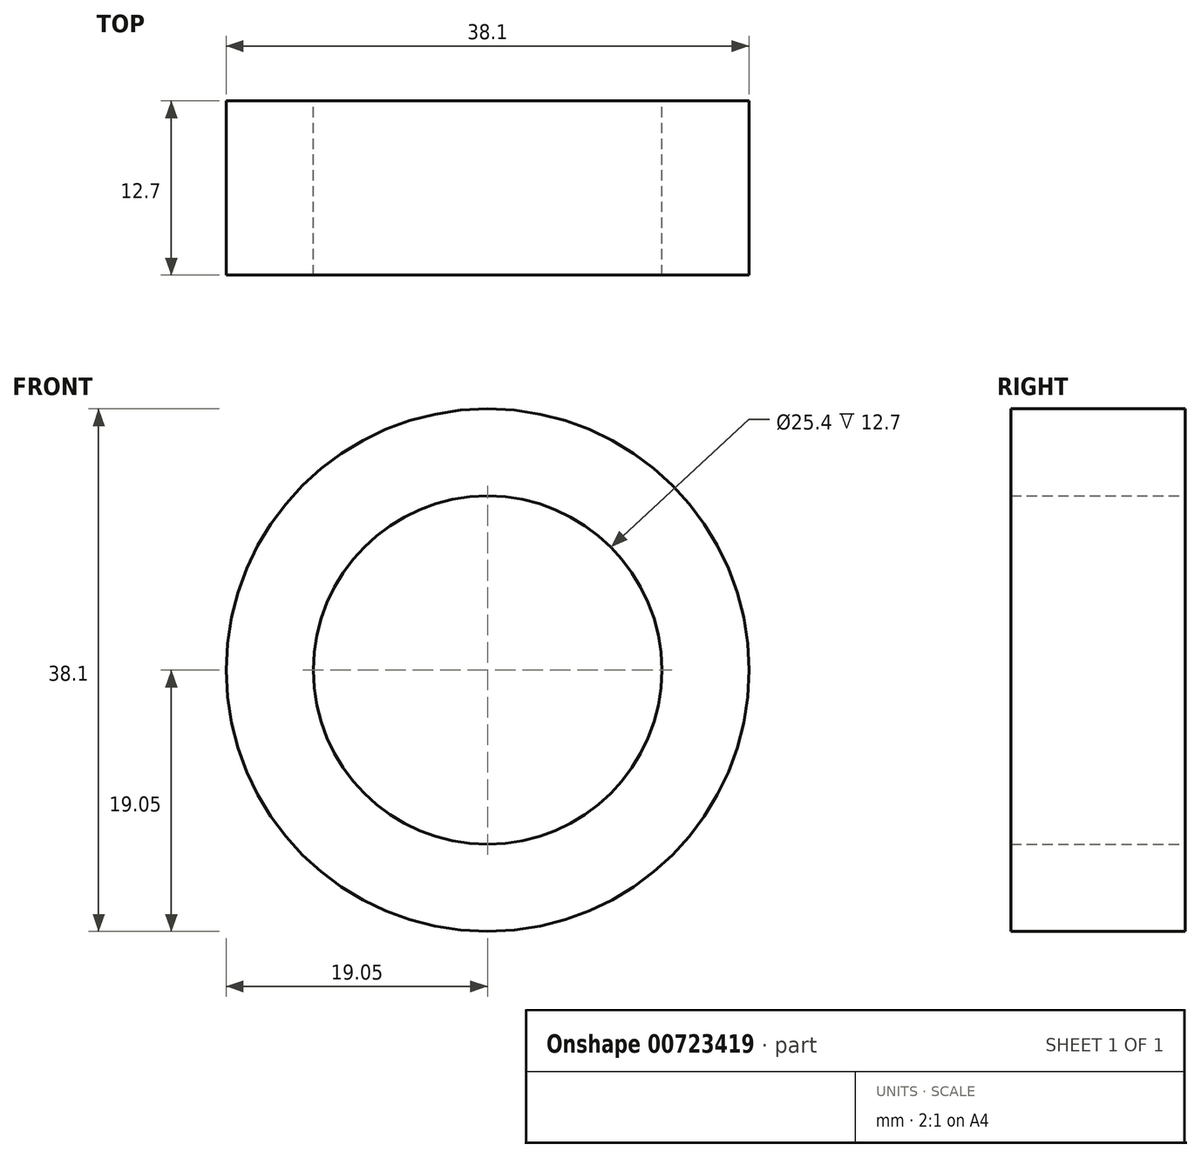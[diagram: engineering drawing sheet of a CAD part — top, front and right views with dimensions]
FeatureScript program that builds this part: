
annotation { "Feature Type Name" : "Feature", "Feature Type Description" : "" }
export const myFeature = defineFeature(function(context is Context, id is Id, definition is map)
    precondition{}
    {
        {
            var Q0;
            Q0=qCreatedBy(makeId("Front.planeOp"),FACE);
            var sketch = newSketch(context, id + "F0", { "sketchPlane" : qUnion([Q0])});
            skCircle(sketch, "E0", {"center": v(0, 0) * mm, "radius": 12.7 * mm});
            skCircle(sketch, "E1.0", {"center": v(0, 0) * mm, "radius": 19.05 * mm});
            skSolve(sketch);
        }
        {
            var Q0;
            Q0=makeQuery(id+"F0.imprint","IMPRINT",FACE,{"disambiguationData":[TD([[makeQuery(id+"F0.imprint","IMPRINT",EDGE,{"derivedFrom":sQuery(id+"F0.wireOp",EDGE,"E0")}),-1.0]])]});
            extrude(context, id + "F1", {"entities" : qUnion([Q0]), "endBound" : BoundingType.SYMMETRIC, "depth" : 12.7 * mm, "offsetDistance" : 25.4 * mm});
        }
    });
